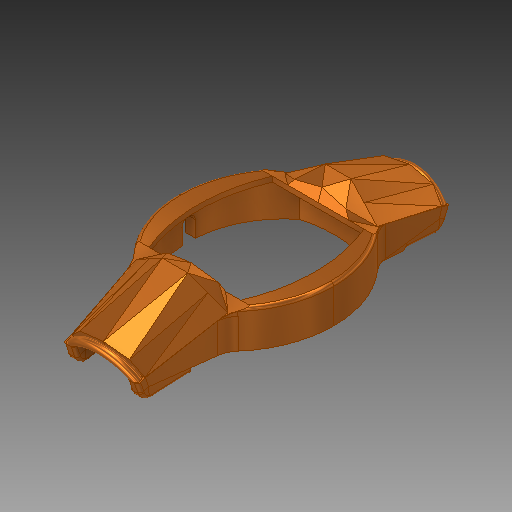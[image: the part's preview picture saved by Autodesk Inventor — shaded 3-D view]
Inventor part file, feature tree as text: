
AUTODESK INVENTOR PART (.ipt)
format: ipt  version: 2019 (Build 230136000, 136)  size: 803,840 bytes
history: native  units: mm
features: other x10, sketch x8, projected_geometry x8, plane x7, extrude x4, fillet x4, sweep x1, revolve x1, hole x1, mirror x1
ambient origin geometry x8: Origin, YZ Plane, XZ Plane, XY Plane, X Axis, Y Axis, Z Axis, Center Point
bodies: Volumenkörper1 (feature_tree), Volumenkörper2 (feature_tree), Volumenkörper3 (feature_tree), Volumenkörper5 (feature_tree)
feature tree (45):
  other  "Körper verschieben1"
  plane  "Arbeitsebene3"
  other  "Trennen1"
  plane  "Arbeitsebene1"
  sketch  "Skizze2"  dims[d2=90.0deg d3=0.8mm]
  plane  "Arbeitsebene2"
  plane  "Arbeitsebene4"
  other  "Trennen2"
  extrude  "Extrusion3"  Depth=0.8mm
  plane  "Arbeitsebene5"
  sweep  "Sweeping2"
  plane  "Arbeitsebene9"
  other  "Trennen5"
  extrude  "Extrusion4"  Depth=0.8mm TaperAngle=0.0deg
  revolve  "Umdrehung2"
  extrude  "Extrusion5"  Depth=0.45mm
  hole  "Bohrung1"  [1 undecoded]
  other  "Mittelebene"
  plane  "Arbeitsebene7"
  other  "Trennen3"
  mirror  "Spiegeln1"
  other  "Mittelebene_2"
  extrude  "Extrusion6"  Depth=3.5mm TaperAngle=0.0deg
  other  "Kombinieren2"
  fillet  "Rundung1"  Radius=1.745329mm
  fillet  "Rundung2"  Radius=6.0mm
  fillet  "Rundung3"  Radius=2.8mm
  fillet  "Rundung4"  Radius=0.5mm
  sketch  "Skizze6"  dims[d13=-3.141593mm d14=-3.141593mm]
  projected_geometry  "Projizierte Kontur4"
  sketch  "Skizze7"  dims[d15=0.0mm d16=0.8mm d17=0.0mm]
  sketch  "Skizze8"  dims[d20=0.0mm d21=0.0mm d22=0.45mm]
  sketch  "Skizze9"  dims[d24=0.45mm d25=1.1mm]
  projected_geometry  "Projizierte Kontur6"
  sketch  "Skizze10"  dims[d26=1.1mm d27=3.5mm d28=0.0mm d29=1.745329mm d30=6.0mm d31=0.0mm]
  projected_geometry  "Projizierte Kontur7"
  projected_geometry  "Projizierte Kontur8"
  sketch  "Skizze11"  dims[d32=1.0mm d33=6.0mm d34=4.0mm d35=2.0mm d36=90.0deg d37=8.0mm d38=20.594885mm d40=2.8mm d41=0.5mm d42=0.0mm]
  projected_geometry  "Projizierte Kontur9"
  sketch  "Skizze13"  dims[d43=2.8mm d44=0.3mm d45=2.5mm d46=1.0mm d47=0.3mm d48=0.0mm]
  projected_geometry  "Projizierte Kontur13"
  projected_geometry  "Projizierte Kontur14"
  projected_geometry  "Projizierte Kontur15"
  other  "brep_1"
  other  "Volumenkörper1:1"
note: 1 required parameter value undecoded (feature->parameter linkage not recoverable at this tier; creation-order binding heuristic only, values carry confidence <= 0.55)
